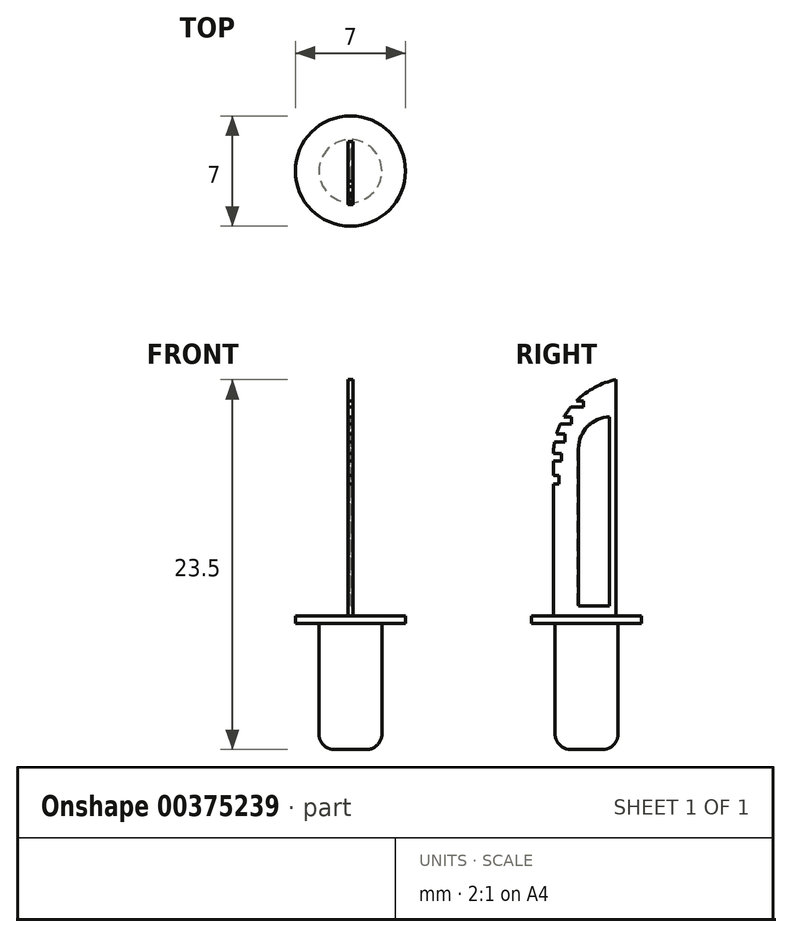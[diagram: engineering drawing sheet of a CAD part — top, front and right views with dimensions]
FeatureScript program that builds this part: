
annotation { "Feature Type Name" : "Feature", "Feature Type Description" : "" }
export const myFeature = defineFeature(function(context is Context, id is Id, definition is map)
    precondition{}
    {
        {
            var Q0;
            Q0=qCreatedBy(makeId("Top.planeOp"),FACE);
            var sketch = newSketch(context, id + "F0", { "sketchPlane" : qUnion([Q0])});
            skCircle(sketch, "E0", {"center": v(0, 0) * mm, "radius": 2 * mm});
            skSolve(sketch);
        }
        {
            var Q0;
            Q0=qSketchRegion(id+"F0",true);
            extrude(context, id + "F1", {"entities" : qUnion([Q0]), "depth" : 8 * mm});
        }
        {
            var Q0;
            Q0=makeQuery(id+"F1.opExtrude","CAP_FACE",FACE,{"disambiguationData":[OSD([sQuery(id+"F0.wireOp",EDGE,"E0")])],"isStart":false});
            var sketch = newSketch(context, id + "F2", { "sketchPlane" : qUnion([Q0])});
            skCircle(sketch, "E1", {"center": v(0, 0) * mm, "radius": 3.5 * mm});
            skSolve(sketch);
        }
        {
            var Q0;
            Q0=makeQuery(id+"F2.imprint","IMPRINT",FACE,{"disambiguationData":[TD([[makeQuery(id+"F2.imprint","IMPRINT",EDGE,{"derivedFrom":sQuery(id+"F2.wireOp",EDGE,"E1")}),1.0]])]});
            var Q1;
            Q1=makeQuery(id+"F2.imprint","IMPRINT",FACE,{"disambiguationData":[TD([[makeQuery(id+"F2.imprint","IMPRINT",EDGE,{"derivedFrom":makeQuery(id+"F1.opExtrude","CAP_EDGE",EDGE,{"disambiguationData":[OSD([sQuery(id+"F0.wireOp",EDGE,"E0")])],"isStart":false})}),1.0]])]});
            extrude(context, id + "F3", {"entities" : qUnion([Q0, Q1]), "operationType" : NewBodyOperationType.ADD, "depth" : .5 * mm});
        }
        {
            var Q0;
            Q0=makeQuery(id+"F3.opExtrude","CAP_FACE",FACE,{"disambiguationData":[OSD([sQuery(id+"F2.wireOp",EDGE,"E1")])],"isStart":false});
            var sketch = newSketch(context, id + "F4", { "sketchPlane" : qUnion([Q0])});
            skLineSegment(sketch, "E2.bottom", {"start": v(-0.15, 1.87) * mm, "end": v(0.15, 1.87) * mm});
            skLineSegment(sketch, "E2.top", {"start": v(-0.15, -2.12) * mm, "end": v(0.15, -2.12) * mm});
            skLineSegment(sketch, "E2.left", {"start": v(-0.15, 1.87) * mm, "end": v(-0.15, -2.12) * mm});
            skLineSegment(sketch, "E2.right", {"start": v(0.15, 1.87) * mm, "end": v(0.15, -2.12) * mm});
            skLineSegment(sketch, "E3", {"start": v(0, 0) * mm, "end": v(0, 3.5) * mm, "construction": true});
            skSolve(sketch);
        }
        {
            var Q0;
            Q0=qSketchRegion(id+"F4",true);
            extrude(context, id + "F5", {"entities" : qUnion([Q0]), "operationType" : NewBodyOperationType.ADD, "depth" : 15 * mm});
        }
        {
            var Q0;
            Q0=makeQuery(id+"F5.opExtrude","CAP_EDGE",EDGE,{"disambiguationData":[OSD([sQuery(id+"F4.wireOp",EDGE,"E2.top")])],"isStart":false});
            fillet(context, id + "F6", {"entities" : qUnion([Q0]), "radius" : 5 * mm, "tangentPropagation" : true, "allowEdgeOverflow" : false});
        }
        {
            var Q0;
            Q0=makeQuery(id+"F1.opExtrude","CAP_EDGE",EDGE,{"disambiguationData":[OSD([sQuery(id+"F0.wireOp",EDGE,"E0")])],"isStart":true});
            fillet(context, id + "F7", {"entities" : qUnion([Q0]), "radius" : 1 * mm, "tangentPropagation" : true, "allowEdgeOverflow" : false});
        }
        {
            var Q0;
            Q0=makeQuery(id+"F5.opExtrude","SWEPT_FACE",FACE,{"disambiguationData":[OSD([sQuery(id+"F4.wireOp",EDGE,"E2.left")])]});
            var sketch = newSketch(context, id + "F8", { "sketchPlane" : qUnion([Q0])});
            skLineSegment(sketch, "E4.bottom", {"start": v(3.03, 20.05) * mm, "end": v(1.38, 20.05) * mm});
            skLineSegment(sketch, "E4.top", {"start": v(3.03, 19.55) * mm, "end": v(1.38, 19.55) * mm});
            skLineSegment(sketch, "E4.left", {"start": v(3.03, 20.05) * mm, "end": v(3.03, 19.55) * mm});
            skLineSegment(sketch, "E4.right", {"start": v(1.38, 20.05) * mm, "end": v(1.38, 19.55) * mm});
            skLineSegment(sketch, "E5.bottom", {"start": v(2.86, 18.8) * mm, "end": v(1.58, 18.8) * mm});
            skLineSegment(sketch, "E5.top", {"start": v(2.86, 18.32) * mm, "end": v(1.58, 18.32) * mm});
            skLineSegment(sketch, "E5.left", {"start": v(2.86, 18.8) * mm, "end": v(2.86, 18.32) * mm});
            skLineSegment(sketch, "E5.right", {"start": v(1.58, 18.8) * mm, "end": v(1.58, 18.32) * mm});
            skLineSegment(sketch, "E6.bottom", {"start": v(2.23, 21.14) * mm, "end": v(0.94, 21.14) * mm});
            skLineSegment(sketch, "E6.top", {"start": v(2.23, 20.68) * mm, "end": v(0.94, 20.68) * mm});
            skLineSegment(sketch, "E6.left", {"start": v(2.23, 21.14) * mm, "end": v(2.23, 20.68) * mm});
            skLineSegment(sketch, "E6.right", {"start": v(0.94, 21.14) * mm, "end": v(0.94, 20.68) * mm});
            skPoint(sketch, "E7.firstSnap0", {"position": v(1, 21.76) * mm});
            skPoint(sketch, "E7.oppositeSnap0", {"position": v(1, 21.76) * mm});
            skLineSegment(sketch, "E7.bottom", {"start": v(1, 22.15) * mm, "end": v(0.2, 22.15) * mm});
            skLineSegment(sketch, "E7.top", {"start": v(1, 21.76) * mm, "end": v(0.2, 21.76) * mm});
            skLineSegment(sketch, "E7.left", {"start": v(1, 22.15) * mm, "end": v(1, 21.76) * mm});
            skLineSegment(sketch, "E7.right", {"start": v(0.2, 22.15) * mm, "end": v(0.2, 21.76) * mm});
            skLineSegment(sketch, "E8.bottom", {"start": v(3.03, 17.42) * mm, "end": v(1.75, 17.42) * mm});
            skLineSegment(sketch, "E8.top", {"start": v(3.03, 16.88) * mm, "end": v(1.75, 16.88) * mm});
            skLineSegment(sketch, "E8.left", {"start": v(3.03, 17.42) * mm, "end": v(3.03, 16.88) * mm});
            skLineSegment(sketch, "E8.right", {"start": v(1.75, 17.42) * mm, "end": v(1.75, 16.88) * mm});
            skSolve(sketch);
        }
        {
            var Q0;
            Q0=qSketchRegion(id+"F8",true);
            extrude(context, id + "F9", {"entities" : qUnion([Q0]), "operationType" : NewBodyOperationType.REMOVE, "oppositeDirection" : true, "depth" : .3 * mm});
        }
        {
            var Q0;
            Q0=makeQuery(id+"F5.opExtrude","SWEPT_FACE",FACE,{"disambiguationData":[OSD([sQuery(id+"F4.wireOp",EDGE,"E2.left")])]});
            var sketch = newSketch(context, id + "F10", { "sketchPlane" : qUnion([Q0])});
            skLineSegment(sketch, "E9.bottom", {"start": v(-1.4, 21.13) * mm, "end": v(-1.4, 21.13) * mm});
            skLineSegment(sketch, "E9.top", {"start": v(-1.4, 9.13) * mm, "end": v(0.6, 9.13) * mm});
            skLineSegment(sketch, "E9.left", {"start": v(-1.4, 21.13) * mm, "end": v(-1.4, 9.13) * mm});
            skLineSegment(sketch, "E9.right", {"start": v(0.6, 19.13) * mm, "end": v(0.6, 9.13) * mm});
            skPoint(sketch, "E10.visualSharp", {"position": v(0.6, 21.13) * mm});
            skArc(sketch, "E10.filletArc", {"start": v(0.6, 19.13) * mm, "mid": v(0.01, 20.54) * mm, "end": v(-1.4, 21.13) * mm});
            skSolve(sketch);
        }
        {
            var Q0;
            Q0=makeQuery(id+"F10.imprint","IMPRINT",FACE,{"disambiguationData":[TD([[makeQuery(id+"F10.imprint","IMPRINT",EDGE,{"derivedFrom":sQuery(id+"F10.wireOp",EDGE,"E9.top")}),1.0]])]});
            extrude(context, id + "F11", {"entities" : qUnion([Q0]), "operationType" : NewBodyOperationType.REMOVE, "oppositeDirection" : true, "depth" : .1 * mm});
        }
        {
            var Q0;
            Q0=makeQuery(id+"F5.opExtrude","SWEPT_FACE",FACE,{"disambiguationData":[OSD([sQuery(id+"F4.wireOp",EDGE,"E2.right")])]});
            var sketch = newSketch(context, id + "F12", { "sketchPlane" : qUnion([Q0])});
            skLineSegment(sketch, "E11.bottom", {"start": v(1.46, 9.11) * mm, "end": v(-0.5, 9.11) * mm});
            skLineSegment(sketch, "E11.top", {"start": v(1.5, 21.13) * mm, "end": v(1.46, 21.13) * mm});
            skLineSegment(sketch, "E11.left", {"start": v(1.46, 9.11) * mm, "end": v(1.46, 21.13) * mm});
            skLineSegment(sketch, "E11.right", {"start": v(-0.5, 9.11) * mm, "end": v(-0.5, 19.13) * mm});
            skPoint(sketch, "E12.visualSharp", {"position": v(-0.5, 21.13) * mm});
            skArc(sketch, "E12.filletArc", {"start": v(1.5, 21.13) * mm, "mid": v(0.08, 20.54) * mm, "end": v(-0.5, 19.13) * mm});
            skSolve(sketch);
        }
        {
            var Q0;
            {var subQ0=sQuery(id+"F12.wireOp",EDGE,"E11.bottom");Q0=makeQuery(id+"F12.imprint","IMPRINT",FACE,{"disambiguationData":[TD([[makeQuery(id+"F12.imprint","IMPRINT",EDGE,{"derivedFrom":subQ0}),-1.0]])]});}
            extrude(context, id + "F13", {"entities" : qUnion([Q0]), "operationType" : NewBodyOperationType.REMOVE, "oppositeDirection" : true, "depth" : .1 * mm});
        }
    });
